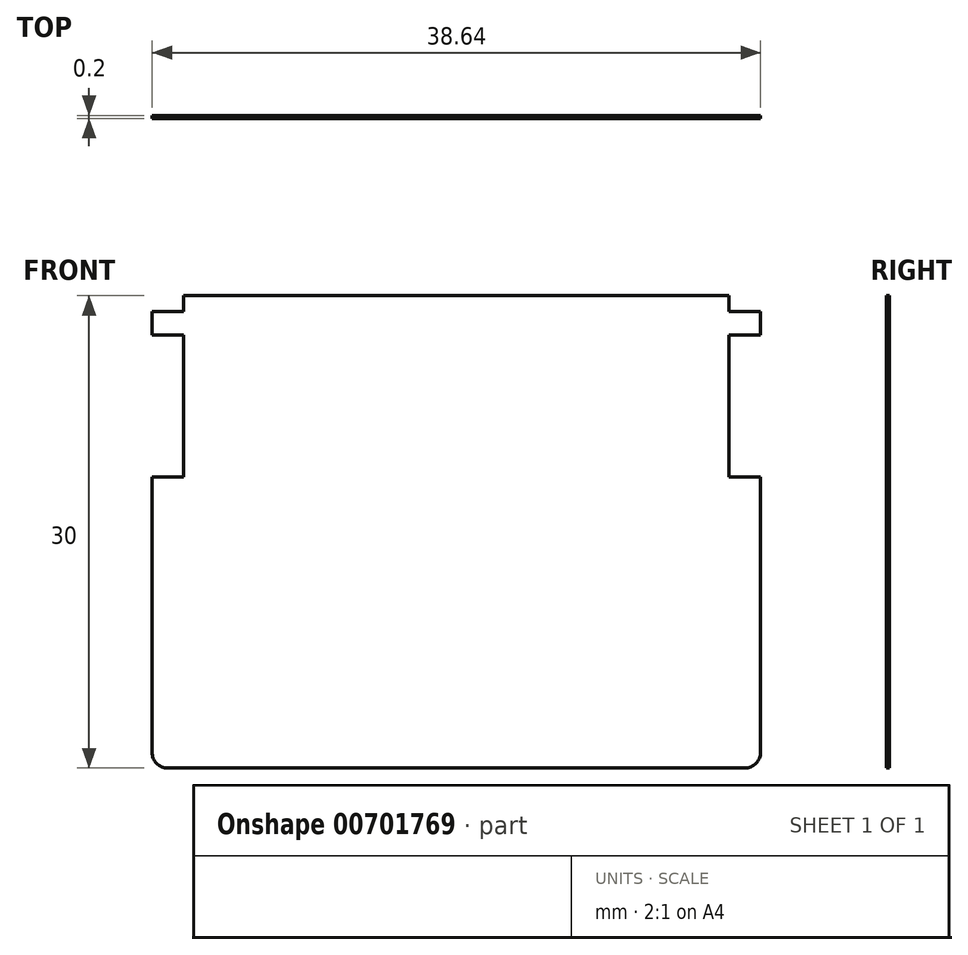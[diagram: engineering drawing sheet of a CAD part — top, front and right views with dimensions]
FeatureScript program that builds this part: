
annotation { "Feature Type Name" : "Feature", "Feature Type Description" : "" }
export const myFeature = defineFeature(function(context is Context, id is Id, definition is map)
    precondition{}
    {
        {
            var Q0;
            Q0=qCreatedBy(makeId("Front.planeOp"),FACE);
            var sketch = newSketch(context, id + "F0", { "sketchPlane" : qUnion([Q0])});
            skPoint(sketch, "E0.middle", {"position": v(0, 0) * mm});
            skLineSegment(sketch, "E1.top", {"start": v(17.32, -2.5) * mm, "end": v(19.33, -2.5) * mm});
            skLineSegment(sketch, "E1.right", {"start": v(19.32, -1) * mm, "end": v(19.32, -2.5) * mm});
            skLineSegment(sketch, "E2.MirrorCS", {"start": v(-19.33, -1) * mm, "end": v(-19.32, -2.5) * mm});
            skLineSegment(sketch, "E3.MirrorCS", {"start": v(-17.32, -2.5) * mm, "end": v(-19.32, -2.5) * mm});
            skPoint(sketch, "E4.positionSnap0", {"position": v(-19.32, -1.75) * mm});
            skLineSegment(sketch, "E5", {"start": v(-19.33, -1) * mm, "end": v(-17.32, -1) * mm});
            skLineSegment(sketch, "E6", {"start": v(-17.32, -1) * mm, "end": v(-17.32, 0) * mm});
            skLineSegment(sketch, "E7", {"start": v(-17.32, 0) * mm, "end": v(17.32, 0) * mm});
            skLineSegment(sketch, "E8", {"start": v(17.32, 0) * mm, "end": v(17.32, -1) * mm});
            skLineSegment(sketch, "E9", {"start": v(17.32, -1) * mm, "end": v(19.33, -1) * mm});
            skLineSegment(sketch, "E10", {"start": v(0, 0) * mm, "end": v(0, -30) * mm, "construction": true});
            skLineSegment(sketch, "E11", {"start": v(-17.33, -2.5) * mm, "end": v(-17.32, -11.5) * mm});
            skLineSegment(sketch, "E12", {"start": v(-17.32, -11.5) * mm, "end": v(-19.33, -11.5) * mm});
            skLineSegment(sketch, "E13", {"start": v(-19.33, -11.5) * mm, "end": v(-19.33, -29) * mm});
            skLineSegment(sketch, "E14", {"start": v(17.32, -2.5) * mm, "end": v(17.33, -11.5) * mm});
            skLineSegment(sketch, "E15", {"start": v(17.32, -11.5) * mm, "end": v(19.33, -11.5) * mm});
            skLineSegment(sketch, "E16", {"start": v(19.32, -11.5) * mm, "end": v(19.32, -29) * mm});
            skLineSegment(sketch, "E17", {"start": v(-18.32, -30) * mm, "end": v(18.32, -30) * mm});
            skPoint(sketch, "E18.visualSharp", {"position": v(-19.33, -30) * mm});
            skArc(sketch, "E18.filletArc", {"start": v(-19.33, -29) * mm, "mid": v(-19.03, -29.7) * mm, "end": v(-18.32, -30) * mm});
            skPoint(sketch, "E19.visualSharp", {"position": v(19.33, -30) * mm});
            skArc(sketch, "E19.filletArc", {"start": v(18.32, -30) * mm, "mid": v(19.03, -29.7) * mm, "end": v(19.33, -29) * mm});
            skSolve(sketch);
        }
        {
            var Q0;
            Q0=makeQuery(id+"F0.imprint","IMPRINT",FACE,{"disambiguationData":[TD([[makeQuery(id+"F0.imprint","IMPRINT",EDGE,{"derivedFrom":sQuery(id+"F0.wireOp",EDGE,"E1.top")}),1.0]])]});
            extrude(context, id + "F1", {"entities" : qUnion([Q0]), "oppositeDirection" : true, "depth" : .2 * mm});
        }
    });
